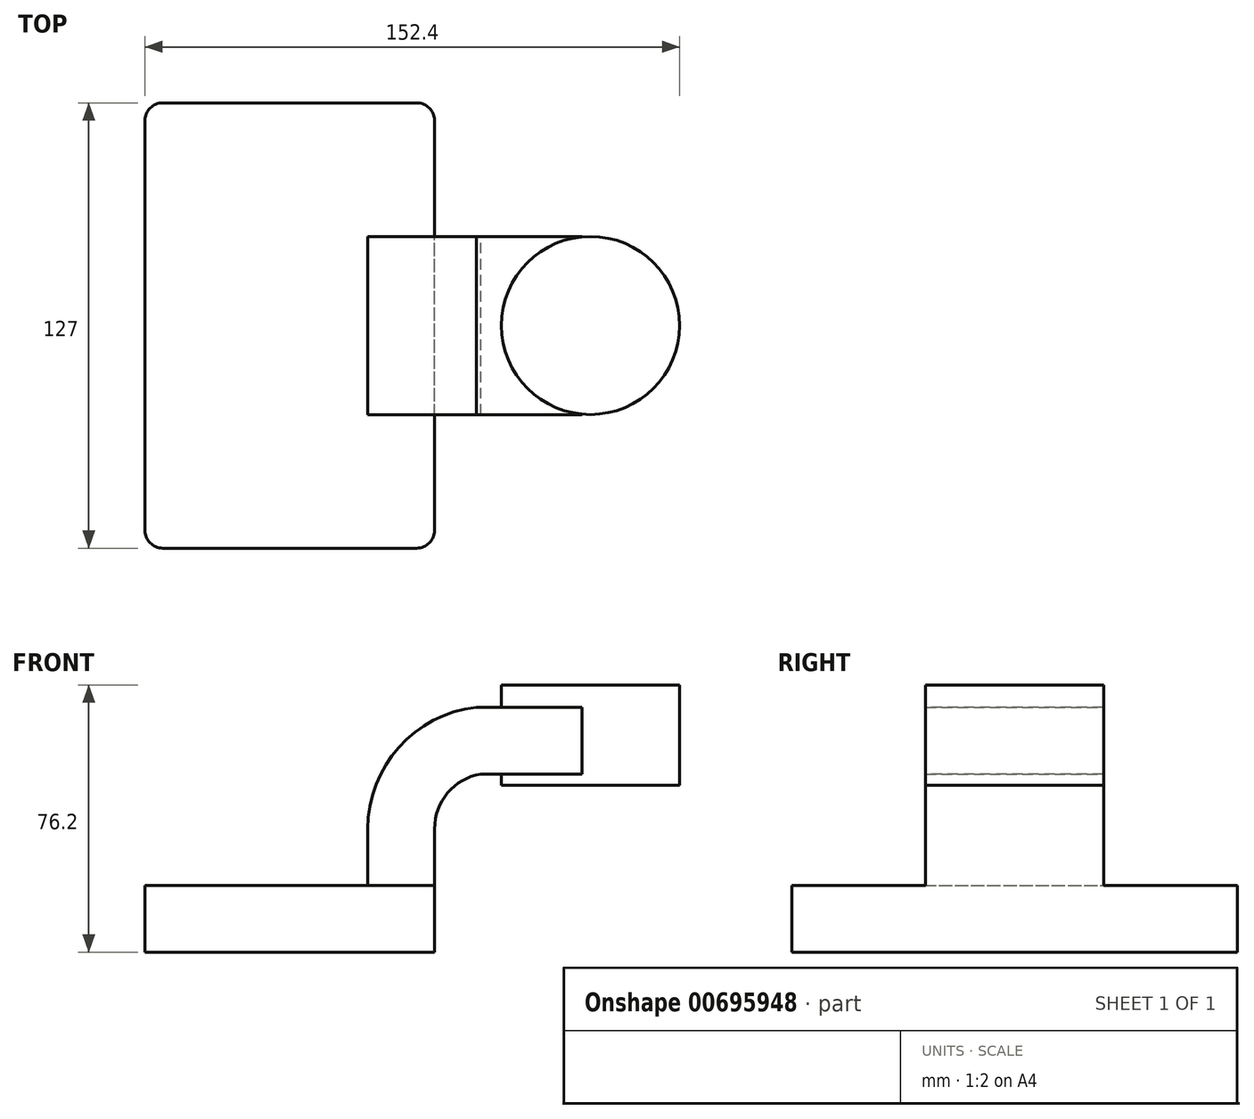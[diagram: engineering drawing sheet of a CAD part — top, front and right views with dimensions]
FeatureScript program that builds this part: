
annotation { "Feature Type Name" : "Feature", "Feature Type Description" : "" }
export const myFeature = defineFeature(function(context is Context, id is Id, definition is map)
    precondition{}
    {
        {
            var Q0;
            Q0=qCreatedBy(makeId("Front.planeOp"),FACE);
            var sketch = newSketch(context, id + "F0", { "sketchPlane" : qUnion([Q0])});
            skLineSegment(sketch, "E0.bottom", {"start": v(-26.87, -19.31) * mm, "end": v(-109.42, -19.31) * mm});
            skLineSegment(sketch, "E0.top", {"start": v(-26.87, -0.26) * mm, "end": v(-109.42, -0.26) * mm});
            skLineSegment(sketch, "E0.left", {"start": v(-26.87, -19.31) * mm, "end": v(-26.87, -0.26) * mm});
            skLineSegment(sketch, "E0.right", {"start": v(-109.42, -19.31) * mm, "end": v(-109.42, -0.26) * mm});
            skPoint(sketch, "E0.middle", {"position": v(-68.14, -9.79) * mm});
            skLineSegment(sketch, "E1.bottom", {"start": v(42.98, 28.31) * mm, "end": v(-7.82, 28.31) * mm});
            skLineSegment(sketch, "E1.top", {"start": v(42.98, 56.89) * mm, "end": v(-7.82, 56.89) * mm});
            skLineSegment(sketch, "E1.left", {"start": v(42.98, 28.31) * mm, "end": v(42.98, 56.89) * mm});
            skLineSegment(sketch, "E1.right", {"start": v(-7.82, 28.31) * mm, "end": v(-7.82, 56.89) * mm});
            skPoint(sketch, "E1.middle", {"position": v(17.58, 42.6) * mm});
            skLineSegment(sketch, "E2", {"start": v(-26.87, -0.26) * mm, "end": v(-26.87, 15.84) * mm});
            skArc(sketch, "E3", {"start": v(-26.87, 15.84) * mm, "mid": v(-23.13, 26.08) * mm, "end": v(-13.67, 31.49) * mm});
            skLineSegment(sketch, "E4", {"start": v(-13.67, 31.49) * mm, "end": v(15.1, 31.49) * mm});
            skLineSegment(sketch, "E5.0", {"start": v(-14.96, 50.54) * mm, "end": v(15.1, 50.54) * mm});
            skArc(sketch, "E5.1", {"start": v(-45.92, 15.84) * mm, "mid": v(-37.06, 39.1) * mm, "end": v(-14.96, 50.54) * mm});
            skLineSegment(sketch, "E5.2", {"start": v(-45.92, -0.26) * mm, "end": v(-45.92, 15.84) * mm});
            skLineSegment(sketch, "E6", {"start": v(17.58, 56.89) * mm, "end": v(17.58, 28.31) * mm});
            skFitSpline(sketch, "E7", {"points": [v(-109.42, -0.26) * mm, v(-14.96, 50.54) * mm], "startDerivative": vector(104.1, 36.79) * mm, "endDerivative": vector(121.2, -0.53) * mm});
            skLineSegment(sketch, "E8", {"start": v(15.1, 50.54) * mm, "end": v(15.1, 31.49) * mm});
            skSolve(sketch);
        }
        {
            var Q0;
            Q0=makeQuery(id+"F0.imprint","IMPRINT",FACE,{"disambiguationData":[TD([[makeQuery(id+"F0.imprint","IMPRINT",EDGE,{"derivedFrom":sQuery(id+"F0.wireOp",EDGE,"E0.bottom")}),-1.0]])]});
            extrude(context, id + "F1", {"entities" : qUnion([Q0]), "endBound" : BoundingType.SYMMETRIC, "depth" : 127 * mm, "offsetDistance" : 25.4 * mm});
        }
        {
            var Q0;
            {var subQ1=sQuery(id+"F0.wireOp",EDGE,"E2");Q0=makeQuery(id+"F0.imprint","IMPRINT",FACE,{"disambiguationData":[TD([[makeQuery(id+"F0.imprint","IMPRINT",EDGE,{"derivedFrom":subQ1}),1.0]])]});}
            var Q1;
            {var subQ5=sQuery(id+"F0.wireOp",EDGE,"E8");Q1=makeQuery(id+"F0.imprint","IMPRINT",FACE,{"disambiguationData":[TD([[makeQuery(id+"F0.imprint","IMPRINT",EDGE,{"derivedFrom":subQ5}),-1.0]])]});}
            extrude(context, id + "F2", {"entities" : qUnion([Q0, Q1]), "operationType" : NewBodyOperationType.ADD, "endBound" : BoundingType.SYMMETRIC, "depth" : 50.8 * mm, "offsetDistance" : 25.4 * mm});
        }
        {
            var Q0;
            Q0=makeQuery(id+"F0.imprint","IMPRINT",FACE,{"disambiguationData":[TD([[makeQuery(id+"F0.imprint","IMPRINT",EDGE,{"derivedFrom":sQuery(id+"F0.wireOp",EDGE,"E5.1")}),1.0]])]});
            extrude(context, id + "F3", {"entities" : qUnion([Q0]), "operationType" : NewBodyOperationType.ADD, "endBound" : BoundingType.SYMMETRIC, "depth" : 19.05 * mm, "offsetDistance" : 25.4 * mm});
        }
        {
            var Q0;
            {var subQ0=sQuery(id+"F0.wireOp",EDGE,"E1.left");Q0=makeQuery(id+"F0.imprint","IMPRINT",FACE,{"disambiguationData":[TD([[makeQuery(id+"F0.imprint","IMPRINT",EDGE,{"derivedFrom":subQ0}),1.0]])]});}
            var Q1;
            Q1=sQuery(id+"F0.wireOp",EDGE,"E6");
            revolve(context, id + "F4", {"operationType" : NewBodyOperationType.ADD, "entities" : qUnion([Q0]), "axis" : qUnion([Q1]), "revolveType" : RevolveType.FULL});
        }
        {
            var Q0;
            Q0=makeQuery(id+"F1.opExtrude","CAP_EDGE",EDGE,{"disambiguationData":[OSD([sQuery(id+"F0.wireOp",EDGE,"E0.right")])],"isStart":false});
            var Q1;
            Q1=makeQuery(id+"F1.opExtrude","CAP_EDGE",EDGE,{"disambiguationData":[OSD([sQuery(id+"F0.wireOp",EDGE,"E0.right")])],"isStart":true});
            var Q2;
            Q2=makeQuery(id+"F1.opExtrude","CAP_EDGE",EDGE,{"disambiguationData":[OSD([sQuery(id+"F0.wireOp",EDGE,"E0.left")])],"isStart":false});
            var Q3;
            Q3=makeQuery(id+"F1.opExtrude","CAP_EDGE",EDGE,{"disambiguationData":[OSD([sQuery(id+"F0.wireOp",EDGE,"E0.left")])],"isStart":true});
            fillet(context, id + "F5", {"entities" : qUnion([Q0, Q1, Q2, Q3]), "radius" : 5.08 * mm, "tangentPropagation" : true, "allowEdgeOverflow" : false});
        }
    });
